# Revit family: Legrand-Enveloppes_industrielles-Metal-Armoires_Altis-P800
name_source: partatom
category: Equipement électrique
units: mm (PartAtom-declared; Revit-internal decimal feet)

## family parameters
Basée sur le plan de construction = Non
Configuration du panneau = Deux colonnes, circuits au sein
Cote de connecteur circulaire = Utiliser le diamètre
Couper avec des vides une fois chargée = Non
Numéro OmniClass = 23.80.30.11.17
Partagée = Non
Point de calcul de pièce = Non
Titre OmniClass = Distribution Boards and Control Panels
Toujours verticalement = Oui
Type d'élément = Tableau de raccordement

## types (7) — shared parameters
Conditions Générale d'Utilisation = https://export.legrand.com
ETIM Class 6.0 = EC000261
Fabricant = Legrand
IK = 10
IP = 55
Matière = Polyester
RAL = 7035
aucun socle = Oui
erreur double hauteur de socle = Non
profondeurprofondeur = 800 mm  [stored 2.62467 ft]
socle 100mm = Non
socle 200mm = Non
zero-valued in all types: Elévation par défaut, hauteur socles

## per-type parameters (varying)
| type | Armoire 047280 | Armoire 047281 | Armoire 047282 | Armoire 047283 | Armoire 047285 | Armoire 047286 | Armoire 047287 | Description | Hauteur | Image du type | Largeur | Poids | URL | distance avant zone d'installation | largeur zone d'installation | profondeur zone d'installation |
| Enveloppe industrielle - Altis - Assemblable - Métal - Profondeur 800mm - Hauteur 2000mm - Largeur  400mm | Oui | Non | Non | Non | Non | Non | Non | Ref 047280 - Enveloppe industrielle - Altis - Assemblable - Métal - Profondeur 800mm | 2023 mm  [stored 6.63714 ft] | Altis_047101_pw_133028_pz_48.jpg | 400 mm  [stored 1.31234 ft] | 3.20 kg | www.legrand.fr | 400 mm  [stored 1.31234 ft] | 2000 mm  [stored 6.56168 ft] | 1200 mm |
| Enveloppe industrielle - Altis - Assemblable - Métal - Profondeur 800mm - Hauteur 2000mm - Largeur  600mm | Non | Oui | Non | Non | Non | Non | Non | Ref 047281 - Enveloppe industrielle - Altis - Assemblable - Métal - Profondeur 800mm | 2023 mm  [stored 6.63714 ft] | Altis_047101_pw_133028_pz_48.jpg | 600 mm | 86.70 kg | www.legrand.fr | 600 mm | 2200 mm | 1400 mm  [stored 4.59318 ft] |
| Enveloppe industrielle - Altis - Assemblable - Métal - Profondeur 800mm - Hauteur 2000mm - Largeur  800mm | Non | Non | Oui | Non | Non | Non | Non | Ref 047282 - Enveloppe industrielle - Altis - Assemblable - Métal - Profondeur 800mm | 2023 mm  [stored 6.63714 ft] | Altis_047101_pw_133028_pz_48.jpg | 800 mm  [stored 2.62467 ft] | 102.20 kg | www.legrand.fr | 800 mm  [stored 2.62467 ft] | 2400 mm | 1600 mm  [stored 5.24934 ft] |
| Enveloppe industrielle - Altis - Assemblable - Métal - Profondeur 800mm - Hauteur 2200mm - Largeur 1000mm - Avec recentrage porte | Non | Non | Non | Oui | Non | Non | Non | Ref 047283 - Enveloppe industrielle - Altis - Assemblable - Métal - Profondeur 800mm | 2023 mm  [stored 6.63714 ft] | Altis_047101_pw_133028_pz_48.jpg | 1000 mm  [stored 3.28084 ft] | 116.80 kg | www.legrand.fr | 1000 mm  [stored 3.28084 ft] | 2600 mm  [stored 8.53018 ft] | 1800 mm  [stored 5.90551 ft] |
| Enveloppe industrielle - Altis - Assemblable - Métal - Profondeur 800mm - Hauteur 2200mm - Largeur 600mm | Non | Non | Non | Non | Oui | Non | Non | Ref 047285 - Enveloppe industrielle - Altis - Assemblable - Métal - Profondeur 800mm | 2223 mm  [stored 7.29331 ft] | <Aucun> | 600 mm | 90.60 kg |  | 600 mm | 2200 mm | 1400 mm  [stored 4.59318 ft] |
| Enveloppe industrielle - Altis - Assemblable - Métal - Profondeur 800mm - Hauteur 2200mm - Largeur 800mm | Non | Non | Non | Non | Non | Oui | Non | Ref 047286 - Enveloppe industrielle - Altis - Assemblable - Métal - Profondeur 800mm | 2223 mm  [stored 7.29331 ft] | Altis_047101_pw_133028_pz_48.jpg | 800 mm  [stored 2.62467 ft] | 107.10 kg | www.legrand.fr | 800 mm  [stored 2.62467 ft] | 2400 mm | 1600 mm  [stored 5.24934 ft] |
| Enveloppe industrielle - Altis - Assemblable - Métal - Profondeur 800mm - Hauteur 2200mm - Largeur 1200mm | Non | Non | Non | Non | Non | Non | Oui | Ref 047287 - Enveloppe industrielle - Altis - Assemblable - Métal - Profondeur 800mm | 2223 mm  [stored 7.29331 ft] | Altis_047101_pw_133028_pz_48.jpg | 1200 mm | 157.30 kg | www.legrand.fr | 1200 mm | 2800 mm  [stored 9.18635 ft] | 2000 mm  [stored 6.56168 ft] |

note: [stored X ft] marks values corroborated as IEEE doubles in the binary element streams (Revit-internal decimal feet)
